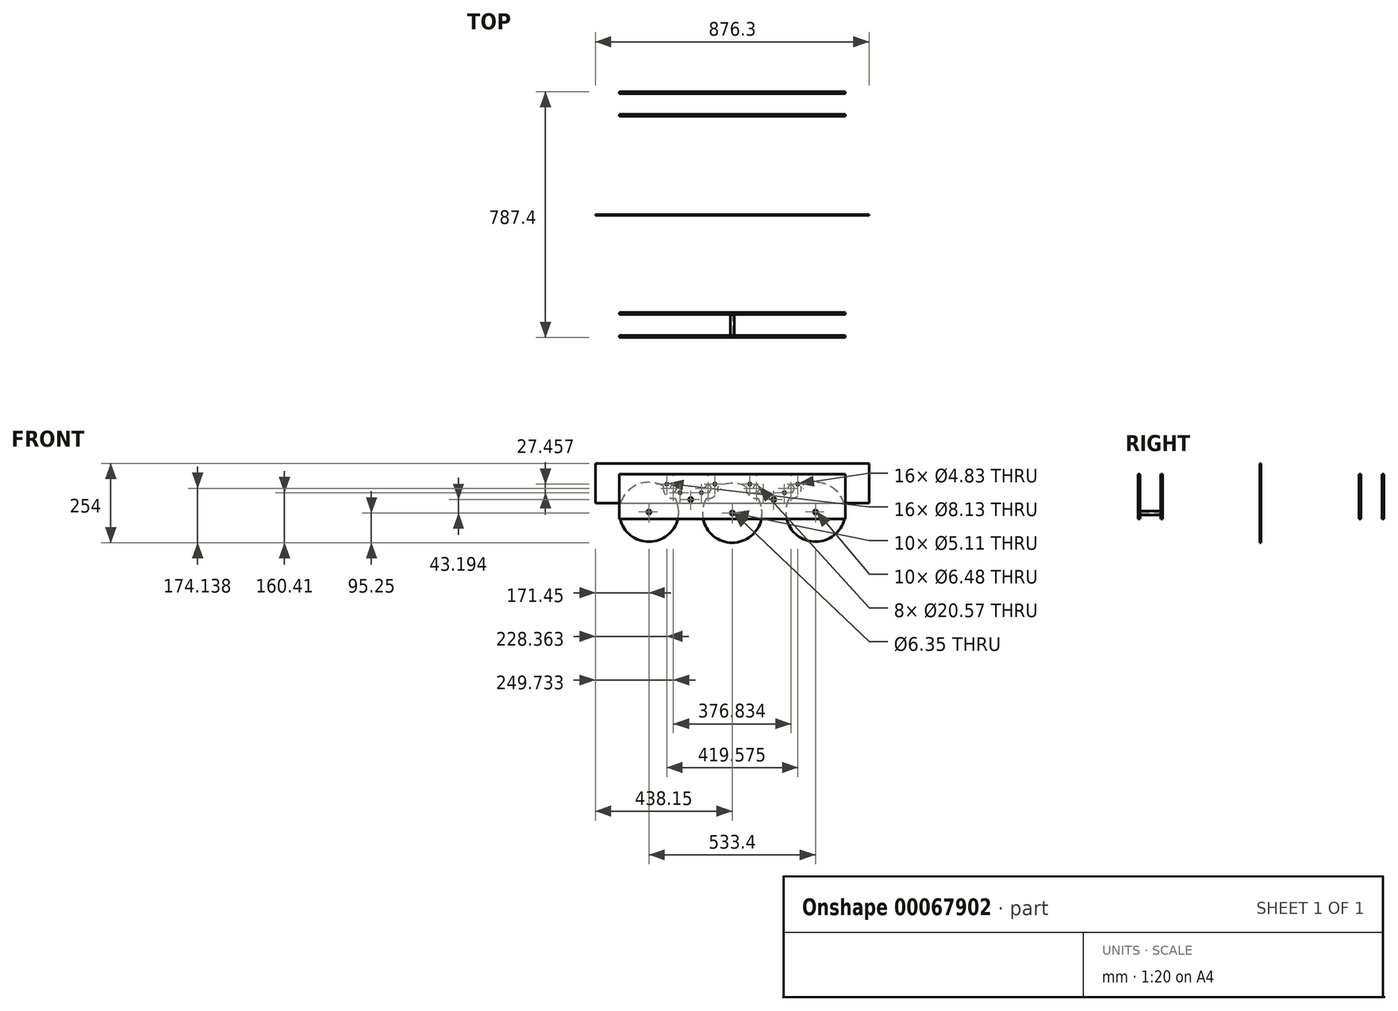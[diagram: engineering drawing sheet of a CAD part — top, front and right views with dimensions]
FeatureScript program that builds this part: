
annotation { "Feature Type Name" : "Feature", "Feature Type Description" : "" }
export const myFeature = defineFeature(function(context is Context, id is Id, definition is map)
    precondition{}
    {
        {
            var Q0;
            Q0=qCreatedBy(makeId("Top.planeOp"),FACE);
            var sketch = newSketch(context, id + "F0", { "sketchPlane" : qUnion([Q0])});
            skLineSegment(sketch, "E0.rect.bottom", {"start": v(361.95, 393.7) * mm, "end": v(-361.95, 393.7) * mm});
            skLineSegment(sketch, "E0.rect.top", {"start": v(361.95, -393.7) * mm, "end": v(-361.95, -393.7) * mm});
            skLineSegment(sketch, "E0.rect.left", {"start": v(361.95, 393.7) * mm, "end": v(361.95, -393.7) * mm});
            skLineSegment(sketch, "E0.rect.right", {"start": v(-361.95, 393.7) * mm, "end": v(-361.95, -393.7) * mm});
            skPoint(sketch, "E0.rect.middle", {"position": v(0, 0) * mm});
            skLineSegment(sketch, "E1.rect.bottom", {"start": v(438.15, 469.9) * mm, "end": v(-438.15, 469.9) * mm});
            skLineSegment(sketch, "E1.rect.top", {"start": v(438.15, -469.9) * mm, "end": v(-438.15, -469.9) * mm});
            skLineSegment(sketch, "E1.rect.left", {"start": v(438.15, 469.9) * mm, "end": v(438.15, -469.9) * mm});
            skLineSegment(sketch, "E1.rect.right", {"start": v(-438.15, 469.9) * mm, "end": v(-438.15, 190.5) * mm});
            skLineSegment(sketch, "E2", {"start": v(0, 469.9) * mm, "end": v(0, 393.7) * mm, "construction": true});
            skLineSegment(sketch, "E3", {"start": v(361.95, 0) * mm, "end": v(438.15, 0) * mm, "construction": true});
            skLineSegment(sketch, "E4", {"start": v(-1421.16, -939.79) * mm, "end": v(-633.76, -939.79) * mm});
            skLineSegment(sketch, "E5", {"start": v(-633.76, -939.79) * mm, "end": v(90.14, -939.79) * mm});
            skLineSegment(sketch, "E6", {"start": v(-438.15, 190.5) * mm, "end": v(-361.95, 190.5) * mm});
            skLineSegment(sketch, "E7", {"start": v(-438.15, -190.5) * mm, "end": v(-361.95, -190.5) * mm});
            skLineSegment(sketch, "E8.trimOffspring", {"start": v(-438.15, -190.5) * mm, "end": v(-438.15, -469.9) * mm});
            skCircle(sketch, "E9", {"center": v(-720.93, 0) * mm, "radius": 127 * mm});
            skSolve(sketch);
        }
        {
            var Q0;
            Q0=qCreatedBy(makeId("Front.planeOp"),FACE);
            var sketch = newSketch(context, id + "F1", { "sketchPlane" : qUnion([Q0])});
            skLineSegment(sketch, "E10", {"start": v(-635, 0) * mm, "end": v(635, 0) * mm, "construction": true});
            skCircle(sketch, "E11", {"center": v(0, 95.25) * mm, "radius": 95.25 * mm});
            skCircle(sketch, "E12", {"center": v(266.7, 98.43) * mm, "radius": 95.25 * mm});
            skCircle(sketch, "E13", {"center": v(-266.7, 98.43) * mm, "radius": 95.25 * mm});
            skLineSegment(sketch, "E14", {"start": v(0, 0) * mm, "end": v(0, 95.25) * mm, "construction": true});
            skLineSegment(sketch, "E15.bottom", {"start": v(-438.15, 254) * mm, "end": v(438.15, 254) * mm, "construction": true});
            skLineSegment(sketch, "E15.top", {"start": v(-438.15, 127) * mm, "end": v(438.15, 127) * mm, "construction": true});
            skLineSegment(sketch, "E15.left", {"start": v(-438.15, 254) * mm, "end": v(-438.15, 127) * mm, "construction": true});
            skLineSegment(sketch, "E15.right", {"start": v(438.15, 254) * mm, "end": v(438.15, 127) * mm, "construction": true});
            skLineSegment(sketch, "E16", {"start": v(361.95, 254) * mm, "end": v(361.95, 127) * mm, "construction": true});
            skLineSegment(sketch, "E17", {"start": v(-361.95, 254) * mm, "end": v(-361.95, 127) * mm, "construction": true});
            skCircle(sketch, "E18", {"center": v(-266.7, 98.43) * mm, "radius": 82.55 * mm, "construction": true});
            skCircle(sketch, "E19", {"center": v(0, 95.25) * mm, "radius": 82.55 * mm, "construction": true});
            skCircle(sketch, "E20", {"center": v(266.7, 98.43) * mm, "radius": 82.55 * mm, "construction": true});
            skCircle(sketch, "E21", {"center": v(-132.85, 138.44) * mm, "radius": 57.15 * mm, "construction": true});
            skCircle(sketch, "E22", {"center": v(132.85, 138.44) * mm, "radius": 57.15 * mm, "construction": true});
            skLineSegment(sketch, "E23.bottom", {"start": v(-489.88, -25) * mm, "end": v(-375.58, -25) * mm});
            skLineSegment(sketch, "E23.top", {"start": v(-489.88, -139.3) * mm, "end": v(-375.58, -139.3) * mm});
            skLineSegment(sketch, "E23.left", {"start": v(-489.88, -25) * mm, "end": v(-489.88, -139.3) * mm});
            skLineSegment(sketch, "E23.right", {"start": v(-375.58, -25) * mm, "end": v(-375.58, -139.3) * mm});
            skLineSegment(sketch, "E24.bottom", {"start": v(-121.04, -27.55) * mm, "end": v(-82.94, -27.55) * mm});
            skLineSegment(sketch, "E24.top", {"start": v(-121.04, -91.05) * mm, "end": v(-82.94, -91.05) * mm});
            skLineSegment(sketch, "E24.left", {"start": v(-121.04, -27.55) * mm, "end": v(-121.04, -91.05) * mm});
            skLineSegment(sketch, "E24.right", {"start": v(-82.94, -27.55) * mm, "end": v(-82.94, -91.05) * mm});
            skLineSegment(sketch, "E25.bottom", {"start": v(348.86, -91.05) * mm, "end": v(386.96, -91.05) * mm});
            skLineSegment(sketch, "E25.top", {"start": v(348.86, -27.55) * mm, "end": v(386.96, -27.55) * mm});
            skLineSegment(sketch, "E25.left", {"start": v(348.86, -91.05) * mm, "end": v(348.86, -27.55) * mm});
            skLineSegment(sketch, "E25.right", {"start": v(386.96, -91.05) * mm, "end": v(386.96, -27.55) * mm});
            skLineSegment(sketch, "E26.bottom", {"start": v(567.74, -139.92) * mm, "end": v(643.94, -139.92) * mm});
            skLineSegment(sketch, "E26.top", {"start": v(567.74, -216.12) * mm, "end": v(643.94, -216.12) * mm});
            skLineSegment(sketch, "E26.left", {"start": v(567.74, -139.92) * mm, "end": v(567.74, -216.12) * mm});
            skLineSegment(sketch, "E26.right", {"start": v(643.94, -139.92) * mm, "end": v(643.94, -216.12) * mm});
            skLineSegment(sketch, "E27", {"start": v(174.08, 76.2) * mm, "end": v(93.33, 76.2) * mm});
            skCircle(sketch, "E28", {"center": v(-188.42, 174.14) * mm, "radius": 32.39 * mm});
            skLineSegment(sketch, "E29", {"start": v(-209.79, 187.87) * mm, "end": v(-167.05, 160.4) * mm, "construction": true});
            skCircle(sketch, "E30", {"center": v(-188.42, 174.14) * mm, "radius": 8.9 * mm, "construction": true});
            skLineSegment(sketch, "E31", {"start": v(-132.85, 138.44) * mm, "end": v(-132.85, 195.6) * mm, "construction": true});
            skLineSegment(sketch, "E32.MirrorCS", {"start": v(-55.92, 187.87) * mm, "end": v(-98.66, 160.4) * mm, "construction": true});
            skCircle(sketch, "E33.MirrorC", {"center": v(-77.3, 174.14) * mm, "radius": 32.39 * mm});
            skCircle(sketch, "E34.MirrorC", {"center": v(-77.3, 174.14) * mm, "radius": 8.9 * mm, "construction": true});
            skCircle(sketch, "E35.MirrorC", {"center": v(188.42, 174.14) * mm, "radius": 8.9 * mm, "construction": true});
            skCircle(sketch, "E36.MirrorC", {"center": v(188.42, 174.14) * mm, "radius": 32.39 * mm});
            skCircle(sketch, "E37.MirrorC", {"center": v(77.3, 174.14) * mm, "radius": 32.39 * mm});
            skLineSegment(sketch, "E38.MirrorCS", {"start": v(209.79, 187.87) * mm, "end": v(167.05, 160.4) * mm, "construction": true});
            skLineSegment(sketch, "E39.MirrorCS", {"start": v(55.92, 187.87) * mm, "end": v(98.66, 160.4) * mm, "construction": true});
            skCircle(sketch, "E40.MirrorC", {"center": v(77.3, 174.14) * mm, "radius": 8.9 * mm, "construction": true});
            skCircle(sketch, "E41", {"center": v(-188.42, 174.14) * mm, "radius": 10.16 * mm});
            skSolve(sketch);
        }
        {
            var Q0;
            Q0=qCreatedBy(makeId("Front.planeOp"),FACE);
            var sketch = newSketch(context, id + "F2", { "sketchPlane" : qUnion([Q0])});
            skLineSegment(sketch, "E42.bottom", {"start": v(-361.95, 219.22) * mm, "end": v(361.95, 219.22) * mm});
            skLineSegment(sketch, "E42.top", {"start": v(-361.95, 76.2) * mm, "end": v(361.95, 76.2) * mm});
            skLineSegment(sketch, "E42.left", {"start": v(-361.95, 219.22) * mm, "end": v(-361.95, 76.2) * mm});
            skLineSegment(sketch, "E42.right", {"start": v(361.95, 219.22) * mm, "end": v(361.95, 76.2) * mm});
            skCircle(sketch, "E43", {"center": v(0, 95.25) * mm, "radius": 2.55 * mm});
            skCircle(sketch, "E44", {"center": v(266.7, 98.43) * mm, "radius": 2.55 * mm});
            skCircle(sketch, "E45", {"center": v(-266.7, 98.43) * mm, "radius": 2.55 * mm});
            skCircle(sketch, "E46", {"center": v(-132.85, 138.44) * mm, "radius": 2.55 * mm});
            skCircle(sketch, "E47", {"center": v(132.85, 138.44) * mm, "radius": 2.55 * mm});
            skCircle(sketch, "E48", {"center": v(98.66, 160.4) * mm, "radius": 2.41 * mm});
            skCircle(sketch, "E49", {"center": v(55.92, 187.87) * mm, "radius": 2.41 * mm});
            skCircle(sketch, "E50", {"center": v(167.05, 160.4) * mm, "radius": 2.41 * mm});
            skCircle(sketch, "E51", {"center": v(209.79, 187.87) * mm, "radius": 2.41 * mm});
            skCircle(sketch, "E52", {"center": v(-55.92, 187.87) * mm, "radius": 2.41 * mm});
            skCircle(sketch, "E53", {"center": v(-98.66, 160.4) * mm, "radius": 2.41 * mm});
            skCircle(sketch, "E54", {"center": v(-167.05, 160.4) * mm, "radius": 2.41 * mm});
            skCircle(sketch, "E55", {"center": v(-209.79, 187.87) * mm, "radius": 2.41 * mm});
            skCircle(sketch, "E56", {"center": v(188.42, 174.14) * mm, "radius": 10.29 * mm});
            skCircle(sketch, "E57", {"center": v(77.3, 174.14) * mm, "radius": 10.29 * mm});
            skCircle(sketch, "E58", {"center": v(-77.3, 174.14) * mm, "radius": 10.29 * mm});
            skCircle(sketch, "E59", {"center": v(-188.42, 174.14) * mm, "radius": 10.29 * mm});
            skSolve(sketch);
        }
        {
            var Q0;
            Q0=makeQuery(id+"F2.imprint","IMPRINT",FACE,{"disambiguationData":[TD([[makeQuery(id+"F2.imprint","IMPRINT",EDGE,{"derivedFrom":sQuery(id+"F2.wireOp",EDGE,"E42.bottom")}),-1.0]])]});
            extrude(context, id + "F3", {"entities" : qUnion([Q0]), "depth" : 6.35 * mm});
        }
        {
            var Q0;
            Q0=makeQuery(id+"F3.opExtrude","CAP_FACE",FACE,{"disambiguationData":[OSD([sQuery(id+"F2.wireOp",EDGE,"E42.bottom"),sQuery(id+"F2.wireOp",EDGE,"E42.top"),sQuery(id+"F2.wireOp",EDGE,"E42.left"),sQuery(id+"F2.wireOp",EDGE,"E42.right"),sQuery(id+"F2.wireOp",EDGE,"E43"),sQuery(id+"F2.wireOp",EDGE,"E44"),sQuery(id+"F2.wireOp",EDGE,"E45"),sQuery(id+"F2.wireOp",EDGE,"E46"),sQuery(id+"F2.wireOp",EDGE,"E47"),sQuery(id+"F2.wireOp",EDGE,"E48"),sQuery(id+"F2.wireOp",EDGE,"E49"),sQuery(id+"F2.wireOp",EDGE,"E50"),sQuery(id+"F2.wireOp",EDGE,"E51"),sQuery(id+"F2.wireOp",EDGE,"E52"),sQuery(id+"F2.wireOp",EDGE,"E53"),sQuery(id+"F2.wireOp",EDGE,"E54"),sQuery(id+"F2.wireOp",EDGE,"E55"),sQuery(id+"F2.wireOp",EDGE,"E56"),sQuery(id+"F2.wireOp",EDGE,"E57"),sQuery(id+"F2.wireOp",EDGE,"E58"),sQuery(id+"F2.wireOp",EDGE,"E59")])],"isStart":false});
            cPlane(context, id + "F4", {"entities" : qUnion([Q0]), "cplaneType" : CPlaneType.OFFSET, "offset" : 66.67 * mm, "width" : 152.4 * mm, "height" : 152.4 * mm});
        }
        {
            var Q0;
            Q0=qCreatedBy(id+"F4.planeOp",FACE);
            var sketch = newSketch(context, id + "F5", { "sketchPlane" : qUnion([Q0])});
            skLineSegment(sketch, "E60.0.0", {"start": v(361.95, 219.22) * mm, "end": v(-361.95, 219.22) * mm});
            skLineSegment(sketch, "E60.0.1", {"start": v(-361.95, 219.22) * mm, "end": v(-361.95, 76.2) * mm});
            skLineSegment(sketch, "E60.0.2", {"start": v(-361.95, 76.2) * mm, "end": v(361.95, 76.2) * mm});
            skLineSegment(sketch, "E60.0.3", {"start": v(361.95, 76.2) * mm, "end": v(361.95, 219.22) * mm});
            skCircle(sketch, "E61.0", {"center": v(-266.7, 98.43) * mm, "radius": 2.55 * mm, "construction": true});
            skCircle(sketch, "E61.1", {"center": v(0, 95.25) * mm, "radius": 2.55 * mm, "construction": true});
            skCircle(sketch, "E61.2", {"center": v(266.7, 98.43) * mm, "radius": 2.55 * mm, "construction": true});
            skCircle(sketch, "E61.3", {"center": v(132.85, 138.44) * mm, "radius": 2.55 * mm, "construction": true});
            skCircle(sketch, "E61.4", {"center": v(-132.85, 138.44) * mm, "radius": 2.55 * mm, "construction": true});
            skCircle(sketch, "E61.5", {"center": v(-98.66, 160.4) * mm, "radius": 2.41 * mm, "construction": true});
            skCircle(sketch, "E61.6", {"center": v(-167.05, 160.4) * mm, "radius": 2.41 * mm, "construction": true});
            skCircle(sketch, "E61.7", {"center": v(-209.79, 187.87) * mm, "radius": 2.41 * mm, "construction": true});
            skCircle(sketch, "E61.8", {"center": v(-55.92, 187.87) * mm, "radius": 2.41 * mm, "construction": true});
            skCircle(sketch, "E61.9", {"center": v(55.92, 187.87) * mm, "radius": 2.41 * mm, "construction": true});
            skCircle(sketch, "E61.10", {"center": v(98.66, 160.4) * mm, "radius": 2.41 * mm, "construction": true});
            skCircle(sketch, "E61.11", {"center": v(167.05, 160.4) * mm, "radius": 2.41 * mm, "construction": true});
            skCircle(sketch, "E61.12", {"center": v(209.79, 187.87) * mm, "radius": 2.41 * mm, "construction": true});
            skCircle(sketch, "E62", {"center": v(-266.7, 98.43) * mm, "radius": 3.24 * mm});
            skCircle(sketch, "E63", {"center": v(-132.85, 138.44) * mm, "radius": 3.24 * mm});
            skCircle(sketch, "E64", {"center": v(0, 95.25) * mm, "radius": 3.24 * mm});
            skCircle(sketch, "E65", {"center": v(132.85, 138.44) * mm, "radius": 3.24 * mm});
            skCircle(sketch, "E66", {"center": v(266.7, 98.43) * mm, "radius": 3.24 * mm});
            skCircle(sketch, "E67", {"center": v(167.05, 160.4) * mm, "radius": 4.06 * mm});
            skCircle(sketch, "E68", {"center": v(98.66, 160.4) * mm, "radius": 4.06 * mm});
            skCircle(sketch, "E69", {"center": v(209.79, 187.87) * mm, "radius": 4.06 * mm});
            skCircle(sketch, "E70", {"center": v(55.92, 187.87) * mm, "radius": 4.06 * mm});
            skCircle(sketch, "E71", {"center": v(-98.66, 160.4) * mm, "radius": 4.06 * mm});
            skCircle(sketch, "E72", {"center": v(-55.92, 187.87) * mm, "radius": 4.06 * mm});
            skCircle(sketch, "E73", {"center": v(-167.05, 160.4) * mm, "radius": 4.06 * mm});
            skCircle(sketch, "E74", {"center": v(-209.79, 187.87) * mm, "radius": 4.06 * mm});
            skSolve(sketch);
        }
        {
            var Q0;
            Q0=makeQuery(id+"F5.imprint","IMPRINT",FACE,{"disambiguationData":[TD([[makeQuery(id+"F5.imprint","IMPRINT",EDGE,{"derivedFrom":sQuery(id+"F5.wireOp",EDGE,"E60.0.0")}),1.0]])]});
            extrude(context, id + "F6", {"entities" : qUnion([Q0]), "depth" : 6.35 * mm});
        }
        {
            var Q0;
            Q0=makeQuery(id+"F6.opExtrude","CAP_FACE",FACE,{"disambiguationData":[OSD([sQuery(id+"F5.wireOp",EDGE,"E60.0.0"),sQuery(id+"F5.wireOp",EDGE,"E60.0.1"),sQuery(id+"F5.wireOp",EDGE,"E60.0.2"),sQuery(id+"F5.wireOp",EDGE,"E60.0.3"),sQuery(id+"F5.wireOp",EDGE,"E62"),sQuery(id+"F5.wireOp",EDGE,"E63"),sQuery(id+"F5.wireOp",EDGE,"E64"),sQuery(id+"F5.wireOp",EDGE,"E65"),sQuery(id+"F5.wireOp",EDGE,"E66"),sQuery(id+"F5.wireOp",EDGE,"E67"),sQuery(id+"F5.wireOp",EDGE,"E68"),sQuery(id+"F5.wireOp",EDGE,"E69"),sQuery(id+"F5.wireOp",EDGE,"E70"),sQuery(id+"F5.wireOp",EDGE,"E71"),sQuery(id+"F5.wireOp",EDGE,"E72"),sQuery(id+"F5.wireOp",EDGE,"E73"),sQuery(id+"F5.wireOp",EDGE,"E74")])],"isStart":false});
            var sketch = newSketch(context, id + "F7", { "sketchPlane" : qUnion([Q0])});
            skCircle(sketch, "E75.0", {"center": v(266.7, 98.43) * mm, "radius": 3.24 * mm});
            skCircle(sketch, "E75.1", {"center": v(0, 95.25) * mm, "radius": 3.24 * mm});
            skCircle(sketch, "E75.2", {"center": v(132.85, 138.44) * mm, "radius": 3.24 * mm});
            skCircle(sketch, "E75.3", {"center": v(-132.85, 138.44) * mm, "radius": 3.24 * mm});
            skCircle(sketch, "E75.4", {"center": v(-266.7, 98.43) * mm, "radius": 3.24 * mm});
            skSolve(sketch);
        }
        {
            var Q0;
            Q0=sQuery(id+"F7.wireOp",VERTEX,"E75.4.center");
            var Q1;
            Q1=sQuery(id+"F7.wireOp",VERTEX,"E75.3.center");
            var Q2;
            Q2=sQuery(id+"F7.wireOp",VERTEX,"E75.1.center");
            var Q3;
            Q3=sQuery(id+"F7.wireOp",VERTEX,"E75.2.center");
            var Q4;
            Q4=sQuery(id+"F7.wireOp",VERTEX,"E75.0.center");
            var Q5;
            Q5=makeQuery(id+"F6.opExtrude","SWEPT_BODY",BODY,{"disambiguationData":[OSD([sQuery(id+"F5.wireOp",EDGE,"E60.0.0"),sQuery(id+"F5.wireOp",EDGE,"E60.0.1"),sQuery(id+"F5.wireOp",EDGE,"E60.0.2"),sQuery(id+"F5.wireOp",EDGE,"E60.0.3"),sQuery(id+"F5.wireOp",EDGE,"E62"),sQuery(id+"F5.wireOp",EDGE,"E63"),sQuery(id+"F5.wireOp",EDGE,"E64"),sQuery(id+"F5.wireOp",EDGE,"E65"),sQuery(id+"F5.wireOp",EDGE,"E66"),sQuery(id+"F5.wireOp",EDGE,"E67"),sQuery(id+"F5.wireOp",EDGE,"E68"),sQuery(id+"F5.wireOp",EDGE,"E69"),sQuery(id+"F5.wireOp",EDGE,"E70"),sQuery(id+"F5.wireOp",EDGE,"E71"),sQuery(id+"F5.wireOp",EDGE,"E72"),sQuery(id+"F5.wireOp",EDGE,"E73"),sQuery(id+"F5.wireOp",EDGE,"E74")])]});
            hole(context, id + "F8", {"style" : HoleStyle.C_SINK, "holeDiameter" : 6.35 * mm, "cSinkDiameter" : 13.5 * mm, "endStyle" : HoleEndStyle.THROUGH, "locations" : qUnion([Q0, Q1, Q2, Q3, Q4]), "scope" : qUnion([Q5]), "cSinkAngle" : 90 * degree});
        }
        {
            var Q0;
            Q0=makeQuery(id+"F3.opExtrude","CAP_FACE",FACE,{"disambiguationData":[OSD([sQuery(id+"F2.wireOp",EDGE,"E42.bottom"),sQuery(id+"F2.wireOp",EDGE,"E42.top"),sQuery(id+"F2.wireOp",EDGE,"E42.left"),sQuery(id+"F2.wireOp",EDGE,"E42.right"),sQuery(id+"F2.wireOp",EDGE,"E43"),sQuery(id+"F2.wireOp",EDGE,"E44"),sQuery(id+"F2.wireOp",EDGE,"E45"),sQuery(id+"F2.wireOp",EDGE,"E46"),sQuery(id+"F2.wireOp",EDGE,"E47"),sQuery(id+"F2.wireOp",EDGE,"E48"),sQuery(id+"F2.wireOp",EDGE,"E49"),sQuery(id+"F2.wireOp",EDGE,"E50"),sQuery(id+"F2.wireOp",EDGE,"E51"),sQuery(id+"F2.wireOp",EDGE,"E52"),sQuery(id+"F2.wireOp",EDGE,"E53"),sQuery(id+"F2.wireOp",EDGE,"E54"),sQuery(id+"F2.wireOp",EDGE,"E55"),sQuery(id+"F2.wireOp",EDGE,"E56"),sQuery(id+"F2.wireOp",EDGE,"E57"),sQuery(id+"F2.wireOp",EDGE,"E58"),sQuery(id+"F2.wireOp",EDGE,"E59")])],"isStart":false});
            var sketch = newSketch(context, id + "F9", { "sketchPlane" : qUnion([Q0])});
            skCircle(sketch, "E76", {"center": v(0, 95.25) * mm, "radius": 6.35 * mm});
            skCircle(sketch, "E77", {"center": v(0, 95.25) * mm, "radius": 3.18 * mm});
            skSolve(sketch);
        }
        {
            var Q0;
            Q0 = qSketchRegion(id + "F9", true);
            var Q1;
            Q1=makeQuery(id+"F6.opExtrude","CAP_FACE",FACE,{"disambiguationData":[OSD([sQuery(id+"F5.wireOp",EDGE,"E60.0.0"),sQuery(id+"F5.wireOp",EDGE,"E60.0.1"),sQuery(id+"F5.wireOp",EDGE,"E60.0.2"),sQuery(id+"F5.wireOp",EDGE,"E60.0.3"),sQuery(id+"F5.wireOp",EDGE,"E62"),sQuery(id+"F5.wireOp",EDGE,"E63"),sQuery(id+"F5.wireOp",EDGE,"E64"),sQuery(id+"F5.wireOp",EDGE,"E65"),sQuery(id+"F5.wireOp",EDGE,"E66"),sQuery(id+"F5.wireOp",EDGE,"E67"),sQuery(id+"F5.wireOp",EDGE,"E68"),sQuery(id+"F5.wireOp",EDGE,"E69"),sQuery(id+"F5.wireOp",EDGE,"E70"),sQuery(id+"F5.wireOp",EDGE,"E71"),sQuery(id+"F5.wireOp",EDGE,"E72"),sQuery(id+"F5.wireOp",EDGE,"E73"),sQuery(id+"F5.wireOp",EDGE,"E74")])],"isStart":true});
            extrude(context, id + "F10", {"entities" : qUnion([Q0]), "endBound" : BoundingType.UP_TO_SURFACE, "endBoundEntityFace" : qUnion([Q1]), "depth" : 25.4 * mm});
        }
        {
            var Q0;
            Q0=makeQuery(id+"F10.opExtrude","SWEPT_FACE",FACE,{"disambiguationData":[OSD([sQuery(id+"F9.wireOp",EDGE,"E76")])]});
            chamfer(context, id + "F11", {"entities" : qUnion([Q0]), "width" : 0.5 * mm, "tangentPropagation" : true});
        }
        {
            var Q0;
            {var subQ1=sQuery(id+"F0.wireOp",EDGE,"E0.rect.bottom");Q0=makeQuery(id+"F0.imprint","IMPRINT",FACE,{"disambiguationData":[TD([[makeQuery(id+"F0.imprint","IMPRINT",EDGE,{"derivedFrom":subQ1}),1.0]])]});}
            var sketch = newSketch(context, id + "F12", { "sketchPlane" : qUnion([Q0])});
            skLineSegment(sketch, "E78.0", {"start": v(-361.95, -79.38) * mm, "end": v(361.95, -79.38) * mm});
            skLineSegment(sketch, "E79", {"start": v(0, -79.38) * mm, "end": v(0, -393.7) * mm});
            skSolve(sketch);
        }
        {
            var Q0;
            Q0=makeQuery(id+"F3.opExtrude","SWEPT_BODY",BODY,{"disambiguationData":[OSD([sQuery(id+"F2.wireOp",EDGE,"E42.bottom"),sQuery(id+"F2.wireOp",EDGE,"E42.top"),sQuery(id+"F2.wireOp",EDGE,"E42.left"),sQuery(id+"F2.wireOp",EDGE,"E42.right"),sQuery(id+"F2.wireOp",EDGE,"E43"),sQuery(id+"F2.wireOp",EDGE,"E44"),sQuery(id+"F2.wireOp",EDGE,"E45"),sQuery(id+"F2.wireOp",EDGE,"E46"),sQuery(id+"F2.wireOp",EDGE,"E47"),sQuery(id+"F2.wireOp",EDGE,"E48"),sQuery(id+"F2.wireOp",EDGE,"E49"),sQuery(id+"F2.wireOp",EDGE,"E50"),sQuery(id+"F2.wireOp",EDGE,"E51"),sQuery(id+"F2.wireOp",EDGE,"E52"),sQuery(id+"F2.wireOp",EDGE,"E53"),sQuery(id+"F2.wireOp",EDGE,"E54"),sQuery(id+"F2.wireOp",EDGE,"E55"),sQuery(id+"F2.wireOp",EDGE,"E56"),sQuery(id+"F2.wireOp",EDGE,"E57"),sQuery(id+"F2.wireOp",EDGE,"E58"),sQuery(id+"F2.wireOp",EDGE,"E59")])]});
            var Q1;
            Q1=makeQuery(id+"F6.opExtrude","SWEPT_BODY",BODY,{"disambiguationData":[OSD([sQuery(id+"F5.wireOp",EDGE,"E60.0.0"),sQuery(id+"F5.wireOp",EDGE,"E60.0.1"),sQuery(id+"F5.wireOp",EDGE,"E60.0.2"),sQuery(id+"F5.wireOp",EDGE,"E60.0.3"),sQuery(id+"F5.wireOp",EDGE,"E62"),sQuery(id+"F5.wireOp",EDGE,"E63"),sQuery(id+"F5.wireOp",EDGE,"E64"),sQuery(id+"F5.wireOp",EDGE,"E65"),sQuery(id+"F5.wireOp",EDGE,"E66"),sQuery(id+"F5.wireOp",EDGE,"E67"),sQuery(id+"F5.wireOp",EDGE,"E68"),sQuery(id+"F5.wireOp",EDGE,"E69"),sQuery(id+"F5.wireOp",EDGE,"E70"),sQuery(id+"F5.wireOp",EDGE,"E71"),sQuery(id+"F5.wireOp",EDGE,"E72"),sQuery(id+"F5.wireOp",EDGE,"E73"),sQuery(id+"F5.wireOp",EDGE,"E74")])]});
            var Q2;
            Q2=makeQuery(id+"F10.opExtrude","SWEPT_BODY",BODY,{"disambiguationData":[OSD([sQuery(id+"F9.wireOp",EDGE,"E76"),sQuery(id+"F9.wireOp",EDGE,"E77")])]});
            var Q3;
            Q3=sQuery(id+"F12.wireOp",EDGE,"E79");
            transform(context, id + "F13", {"entities" : qUnion([Q0, Q1, Q2]), "transformType" : TransformType.TRANSLATION_ENTITY, "oppositeDirectionEntity" : false, "transformLine" : qUnion([Q3]), "makeCopy" : false});
        }
        {
            var Q0;
            Q0=makeQuery(id+"F3.opExtrude","SWEPT_BODY",BODY,{"disambiguationData":[OSD([sQuery(id+"F2.wireOp",EDGE,"E42.bottom"),sQuery(id+"F2.wireOp",EDGE,"E42.top"),sQuery(id+"F2.wireOp",EDGE,"E42.left"),sQuery(id+"F2.wireOp",EDGE,"E42.right"),sQuery(id+"F2.wireOp",EDGE,"E43"),sQuery(id+"F2.wireOp",EDGE,"E44"),sQuery(id+"F2.wireOp",EDGE,"E45"),sQuery(id+"F2.wireOp",EDGE,"E46"),sQuery(id+"F2.wireOp",EDGE,"E47"),sQuery(id+"F2.wireOp",EDGE,"E48"),sQuery(id+"F2.wireOp",EDGE,"E49"),sQuery(id+"F2.wireOp",EDGE,"E50"),sQuery(id+"F2.wireOp",EDGE,"E51"),sQuery(id+"F2.wireOp",EDGE,"E52"),sQuery(id+"F2.wireOp",EDGE,"E53"),sQuery(id+"F2.wireOp",EDGE,"E54"),sQuery(id+"F2.wireOp",EDGE,"E55"),sQuery(id+"F2.wireOp",EDGE,"E56"),sQuery(id+"F2.wireOp",EDGE,"E57"),sQuery(id+"F2.wireOp",EDGE,"E58"),sQuery(id+"F2.wireOp",EDGE,"E59")])]});
            var Q1;
            Q1=makeQuery(id+"F6.opExtrude","SWEPT_BODY",BODY,{"disambiguationData":[OSD([sQuery(id+"F5.wireOp",EDGE,"E60.0.0"),sQuery(id+"F5.wireOp",EDGE,"E60.0.1"),sQuery(id+"F5.wireOp",EDGE,"E60.0.2"),sQuery(id+"F5.wireOp",EDGE,"E60.0.3"),sQuery(id+"F5.wireOp",EDGE,"E62"),sQuery(id+"F5.wireOp",EDGE,"E63"),sQuery(id+"F5.wireOp",EDGE,"E64"),sQuery(id+"F5.wireOp",EDGE,"E65"),sQuery(id+"F5.wireOp",EDGE,"E66"),sQuery(id+"F5.wireOp",EDGE,"E67"),sQuery(id+"F5.wireOp",EDGE,"E68"),sQuery(id+"F5.wireOp",EDGE,"E69"),sQuery(id+"F5.wireOp",EDGE,"E70"),sQuery(id+"F5.wireOp",EDGE,"E71"),sQuery(id+"F5.wireOp",EDGE,"E72"),sQuery(id+"F5.wireOp",EDGE,"E73"),sQuery(id+"F5.wireOp",EDGE,"E74")])]});
            var Q2;
            Q2=qCreatedBy(makeId("Front.planeOp"),FACE);
            mirror(context, id + "F14", {"entities" : qUnion([Q0, Q1]), "mirrorPlane" : qUnion([Q2])});
        }
        {
            var Q0;
            Q0=qCreatedBy(makeId("Front.planeOp"),FACE);
            var sketch = newSketch(context, id + "F15", { "sketchPlane" : qUnion([Q0])});
            skArc(sketch, "E80.0.1", {"start": v(-359.32, 76.2) * mm, "mid": v(-266.7, 3.17) * mm, "end": v(-174.08, 76.2) * mm});
            skArc(sketch, "E80.1.3", {"start": v(-93.33, 76.2) * mm, "mid": v(0, 0) * mm, "end": v(93.33, 76.2) * mm});
            skArc(sketch, "E80.2.2", {"start": v(174.08, 76.2) * mm, "mid": v(266.7, 3.17) * mm, "end": v(359.32, 76.2) * mm});
            skLineSegment(sketch, "E80.3.0", {"start": v(361.95, 76.2) * mm, "end": v(361.95, 219.22) * mm});
            skLineSegment(sketch, "E80.3.1", {"start": v(361.95, 219.22) * mm, "end": v(-361.95, 219.22) * mm});
            skLineSegment(sketch, "E80.3.2", {"start": v(-361.95, 219.22) * mm, "end": v(-361.95, 76.2) * mm});
            skLineSegment(sketch, "E80.3.3", {"start": v(-361.95, 76.2) * mm, "end": v(361.95, 76.2) * mm});
            skPoint(sketch, "E80.2.0.start.orphan", {"position": v(219.97, 181.43) * mm});
            skPoint(sketch, "E80.2.1.start.orphan", {"position": v(182.19, 142.36) * mm});
            skPoint(sketch, "E80.1.0.start.orphan", {"position": v(82.86, 142.23) * mm});
            skPoint(sketch, "E80.1.1.start.orphan", {"position": v(45.28, 179.05) * mm});
            skPoint(sketch, "E80.1.2.start.orphan", {"position": v(-45.28, 179.05) * mm});
            skPoint(sketch, "E81.orphan", {"position": v(-82.86, 142.23) * mm});
            skPoint(sketch, "E80.0.0.start.orphan", {"position": v(-182.19, 142.36) * mm});
            skPoint(sketch, "E82.orphan", {"position": v(-219.97, 181.43) * mm});
            skLineSegment(sketch, "E83.0", {"start": v(-438.15, 127) * mm, "end": v(438.15, 127) * mm});
            skLineSegment(sketch, "E84.0", {"start": v(-438.15, 254) * mm, "end": v(438.15, 254) * mm});
            skLineSegment(sketch, "E84.1", {"start": v(-438.15, 254) * mm, "end": v(-438.15, 127) * mm});
            skLineSegment(sketch, "E84.2", {"start": v(438.15, 254) * mm, "end": v(438.15, 127) * mm});
            skSolve(sketch);
        }
        {
            var Q0;
            {var subQ4=sQuery(id+"F15.wireOp",EDGE,"E80.3.1");Q0=makeQuery(id+"F15.imprint","IMPRINT",FACE,{"disambiguationData":[TD([[makeQuery(id+"F15.imprint","IMPRINT",EDGE,{"derivedFrom":subQ4}),-1.0]])]});}
            var Q1;
            {var subQ0=sQuery(id+"F15.wireOp",EDGE,"E80.3.1");Q1=makeQuery(id+"F15.imprint","IMPRINT",FACE,{"disambiguationData":[TD([[makeQuery(id+"F15.imprint","IMPRINT",EDGE,{"derivedFrom":subQ0}),1.0]])]});}
            var Q2;
            {var subQ0=sQuery(id+"F1.wireOp",EDGE,"E28");var subQ1=sQuery(id+"F1.wireOp",EDGE,"E13");var subQ2=makeQuery(id+"F1.imprint","INTERSECT",VERTEX,{"disambiguationData":[OD(0.0)],"derivedFrom":[subQ1,subQ0]});Q2=makeQuery(id+"F1.imprint","IMPRINT",FACE,{"disambiguationData":[TD([[makeQuery(id+"F1.imprint","IMPRINT",EDGE,{"disambiguationData":[TD([[subQ2,-1.0]])],"derivedFrom":subQ1}),1.0]])]});}
            var Q3;
            {var subQ0=sQuery(id+"F15.wireOp",EDGE,"E80.1.3");Q3=makeQuery(id+"F15.imprint","IMPRINT",FACE,{"disambiguationData":[TD([[makeQuery(id+"F15.imprint","IMPRINT",EDGE,{"derivedFrom":subQ0}),1.0]])]});}
            var Q4;
            {var subQ0=sQuery(id+"F15.wireOp",EDGE,"E80.2.2");Q4=makeQuery(id+"F15.imprint","IMPRINT",FACE,{"disambiguationData":[TD([[makeQuery(id+"F15.imprint","IMPRINT",EDGE,{"derivedFrom":subQ0}),1.0]])]});}
            var Q5;
            {var subQ0=sQuery(id+"F1.wireOp",EDGE,"E12");var subQ1=makeQuery(id+"F1.imprint","IMPRINT",VERTEX,{"derivedFrom":subQ0});Q5=makeQuery(id+"F1.imprint","IMPRINT",FACE,{"disambiguationData":[TD([[makeQuery(id+"F1.imprint","IMPRINT",EDGE,{"disambiguationData":[TD([[subQ1,1.0]])],"derivedFrom":subQ0}),1.0]])]});}
            var Q6;
            {var subQ1=sQuery(id+"F1.wireOp",EDGE,"E11");var subQ4=makeQuery(id+"F1.imprint","IMPRINT",VERTEX,{"derivedFrom":subQ1});Q6=makeQuery(id+"F1.imprint","IMPRINT",FACE,{"disambiguationData":[TD([[makeQuery(id+"F1.imprint","IMPRINT",EDGE,{"disambiguationData":[TD([[subQ4,1.0]])],"derivedFrom":subQ1}),1.0]])]});}
            extrude(context, id + "F16", {"entities" : qUnion([Q0, Q1, Q2, Q3, Q4, Q5, Q6]), "operationType" : NewBodyOperationType.ADD, "depth" : 3.17 * mm});
        }
    });
